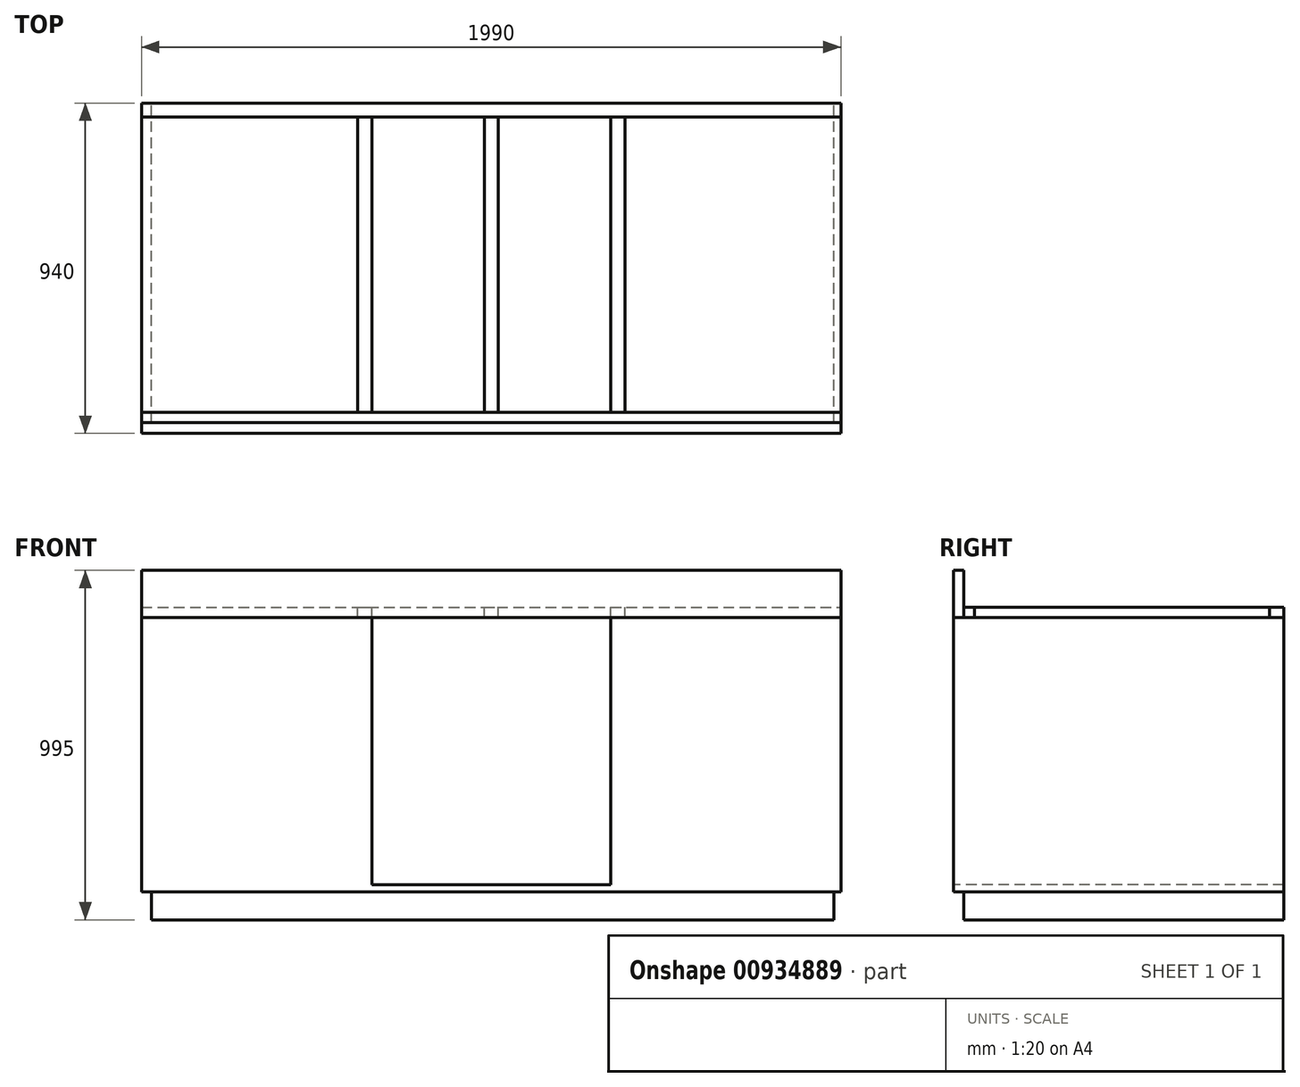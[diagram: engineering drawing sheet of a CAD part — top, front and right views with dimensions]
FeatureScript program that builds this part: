
annotation { "Feature Type Name" : "Feature", "Feature Type Description" : "" }
export const myFeature = defineFeature(function(context is Context, id is Id, definition is map)
    precondition{}
    {
        {
            var Q0;
            Q0=qCreatedBy(makeId("Front.planeOp"),FACE);
            var sketch = newSketch(context, id + "F0", { "sketchPlane" : qUnion([Q0])});
            skLineSegment(sketch, "E0.bottom", {"start": v(0, 0) * mm, "end": v(-655, 0) * mm});
            skLineSegment(sketch, "E0.top", {"start": v(0, 780) * mm, "end": v(-655, 780) * mm});
            skLineSegment(sketch, "E0.left", {"start": v(0, 0) * mm, "end": v(0, 780) * mm});
            skLineSegment(sketch, "E0.right", {"start": v(-655, 0) * mm, "end": v(-655, 780) * mm});
            skLineSegment(sketch, "E1.bottom", {"start": v(-655, 0) * mm, "end": v(-1335, 0) * mm});
            skLineSegment(sketch, "E1.top", {"start": v(-655, 20) * mm, "end": v(-1335, 20) * mm});
            skLineSegment(sketch, "E1.left", {"start": v(-655, 0) * mm, "end": v(-655, 20) * mm});
            skLineSegment(sketch, "E1.right", {"start": v(-1335, 0) * mm, "end": v(-1335, 20) * mm});
            skLineSegment(sketch, "E2.bottom", {"start": v(-1335, 0) * mm, "end": v(-1990, 0) * mm});
            skLineSegment(sketch, "E2.top", {"start": v(-1335, 780) * mm, "end": v(-1990, 780) * mm});
            skLineSegment(sketch, "E2.left", {"start": v(-1335, 0) * mm, "end": v(-1335, 780) * mm});
            skLineSegment(sketch, "E2.right", {"start": v(-1990, 0) * mm, "end": v(-1990, 780) * mm});
            skLineSegment(sketch, "E3.bottom", {"start": v(0, 780) * mm, "end": v(-1990, 780) * mm});
            skLineSegment(sketch, "E3.top", {"start": v(0, 915) * mm, "end": v(-1990, 915) * mm});
            skLineSegment(sketch, "E3.left", {"start": v(0, 780) * mm, "end": v(0, 915) * mm});
            skLineSegment(sketch, "E3.right", {"start": v(-1990, 780) * mm, "end": v(-1990, 915) * mm});
            skSolve(sketch);
        }
        {
            var Q0;
            Q0=makeQuery(id+"F0.imprint","IMPRINT",FACE,{"disambiguationData":[TD([[makeQuery(id+"F0.imprint","IMPRINT",EDGE,{"derivedFrom":sQuery(id+"F0.wireOp",EDGE,"E0.bottom")}),-1.0]])]});
            var Q1;
            {var subQ5=sQuery(id+"F0.wireOp",EDGE,"E2.bottom");Q1=makeQuery(id+"F0.imprint","IMPRINT",FACE,{"disambiguationData":[TD([[makeQuery(id+"F0.imprint","IMPRINT",EDGE,{"derivedFrom":subQ5}),-1.0]])]});}
            var Q2;
            {var subQ0=sQuery(id+"F0.wireOp",EDGE,"E1.bottom");Q2=makeQuery(id+"F0.imprint","IMPRINT",FACE,{"disambiguationData":[TD([[makeQuery(id+"F0.imprint","IMPRINT",EDGE,{"derivedFrom":subQ0}),-1.0]])]});}
            var Q3;
            Q3=sQuery(id+"F0.wireOp",EDGE,"E0.right");
            var Q4;
            Q4=sQuery(id+"F0.wireOp",EDGE,"E0.top");
            var Q5;
            Q5=sQuery(id+"F0.wireOp",EDGE,"E0.left");
            var Q6;
            Q6=sQuery(id+"F0.wireOp",EDGE,"E0.bottom");
            extrude(context, id + "F1", {"entities" : qUnion([Q0, Q1, Q2]), "surfaceEntities" : qUnion([Q3, Q4, Q5, Q6]), "oppositeDirection" : true, "depth" : 940 * mm, "offsetDistance" : 25 * mm});
        }
        {
            var Q0;
            Q0=makeQuery(id+"F0.imprint","IMPRINT",FACE,{"disambiguationData":[TD([[makeQuery(id+"F0.imprint","IMPRINT",EDGE,{"derivedFrom":sQuery(id+"F0.wireOp",EDGE,"E3.top")}),1.0]])]});
            extrude(context, id + "F2", {"entities" : qUnion([Q0]), "oppositeDirection" : true, "depth" : 30 * mm, "offsetDistance" : 25 * mm});
        }
        {
            var Q0;
            Q0=makeQuery(id+"F2.opExtrude","SWEPT_FACE",FACE,{"disambiguationData":[OSD([sQuery(id+"F0.wireOp",EDGE,"E3.left")])]});
            var sketch = newSketch(context, id + "F3", { "sketchPlane" : qUnion([Q0])});
            skLineSegment(sketch, "E4.bottom", {"start": v(30, 780) * mm, "end": v(60, 780) * mm});
            skLineSegment(sketch, "E4.top", {"start": v(30, 810) * mm, "end": v(60, 810) * mm});
            skLineSegment(sketch, "E4.left", {"start": v(30, 780) * mm, "end": v(30, 810) * mm});
            skLineSegment(sketch, "E4.right", {"start": v(60, 780) * mm, "end": v(60, 810) * mm});
            skLineSegment(sketch, "E5.bottom", {"start": v(940, 780) * mm, "end": v(900, 780) * mm});
            skLineSegment(sketch, "E5.top", {"start": v(940, 810) * mm, "end": v(900, 810) * mm});
            skLineSegment(sketch, "E5.left", {"start": v(940, 780) * mm, "end": v(940, 810) * mm});
            skLineSegment(sketch, "E5.right", {"start": v(900, 780) * mm, "end": v(900, 810) * mm});
            skSolve(sketch);
        }
        {
            var Q0;
            Q0 = qSketchRegion(id + "F3", true);
            var Q1;
            Q1=makeQuery(id+"F1.opExtrude","SWEPT_FACE",FACE,{"disambiguationData":[OSD([sQuery(id+"F0.wireOp",EDGE,"E2.right")])]});
            extrude(context, id + "F4", {"entities" : qUnion([Q0]), "endBound" : BoundingType.UP_TO_SURFACE, "oppositeDirection" : true, "depth" : 25 * mm, "endBoundEntityFace" : qUnion([Q1]), "offsetDistance" : 25 * mm});
        }
        {
            var Q0;
            Q0=makeQuery(id+"F4.opExtrude","SWEPT_FACE",FACE,{"disambiguationData":[OSD([sQuery(id+"F3.wireOp",EDGE,"E4.right")])]});
            var sketch = newSketch(context, id + "F5", { "sketchPlane" : qUnion([Q0])});
            skLineSegment(sketch, "E6.bottom", {"start": v(655, 780) * mm, "end": v(615, 780) * mm});
            skLineSegment(sketch, "E6.top", {"start": v(655, 810) * mm, "end": v(615, 810) * mm});
            skLineSegment(sketch, "E6.left", {"start": v(655, 780) * mm, "end": v(655, 810) * mm});
            skLineSegment(sketch, "E6.right", {"start": v(615, 780) * mm, "end": v(615, 810) * mm});
            skLineSegment(sketch, "E7.1.0.0", {"start": v(1015, 780) * mm, "end": v(1015, 810) * mm});
            skLineSegment(sketch, "E7.1.0.1", {"start": v(975, 780) * mm, "end": v(975, 810) * mm});
            skLineSegment(sketch, "E7.1.0.2", {"start": v(1015, 810) * mm, "end": v(975, 810) * mm});
            skLineSegment(sketch, "E7.1.0.3", {"start": v(1015, 780) * mm, "end": v(975, 780) * mm});
            skLineSegment(sketch, "E7.2.0.0", {"start": v(1375, 780) * mm, "end": v(1375, 810) * mm});
            skLineSegment(sketch, "E7.2.0.1", {"start": v(1335, 780) * mm, "end": v(1335, 810) * mm});
            skLineSegment(sketch, "E7.2.0.2", {"start": v(1375, 810) * mm, "end": v(1335, 810) * mm});
            skLineSegment(sketch, "E7.2.0.3", {"start": v(1375, 780) * mm, "end": v(1335, 780) * mm});
            skLineSegment(sketch, "E7.direction1", {"start": v(615, 780) * mm, "end": v(975, 780) * mm, "construction": true});
            skSolve(sketch);
        }
        {
            var Q0;
            Q0 = qSketchRegion(id + "F5", true);
            var Q1;
            Q1=makeQuery(id+"F4.opExtrude","SWEPT_FACE",FACE,{"disambiguationData":[OSD([sQuery(id+"F3.wireOp",EDGE,"E5.right")])]});
            extrude(context, id + "F6", {"entities" : qUnion([Q0]), "endBound" : BoundingType.UP_TO_SURFACE, "depth" : 25 * mm, "endBoundEntityFace" : qUnion([Q1]), "offsetDistance" : 25 * mm});
        }
        {
            var Q0;
            Q0=makeQuery(id+"F1.opExtrude","SWEPT_FACE",FACE,{"disambiguationData":[OSD([sQuery(id+"F0.wireOp",EDGE,"E0.bottom"),sQuery(id+"F0.wireOp",EDGE,"E1.bottom"),sQuery(id+"F0.wireOp",EDGE,"E2.bottom")])]});
            var sketch = newSketch(context, id + "F7", { "sketchPlane" : qUnion([Q0])});
            skLineSegment(sketch, "E8.bottom", {"start": v(-1962, -30) * mm, "end": v(-20, -30) * mm});
            skLineSegment(sketch, "E8.top", {"start": v(-1962, -940) * mm, "end": v(-20, -940) * mm});
            skLineSegment(sketch, "E8.left", {"start": v(-1962, -30) * mm, "end": v(-1962, -940) * mm});
            skLineSegment(sketch, "E8.right", {"start": v(-20, -30) * mm, "end": v(-20, -940) * mm});
            skSolve(sketch);
        }
        {
            var Q0;
            Q0 = qSketchRegion(id + "F7", true);
            extrude(context, id + "F8", {"entities" : qUnion([Q0]), "depth" : 80 * mm, "offsetDistance" : 25 * mm});
        }
    });
